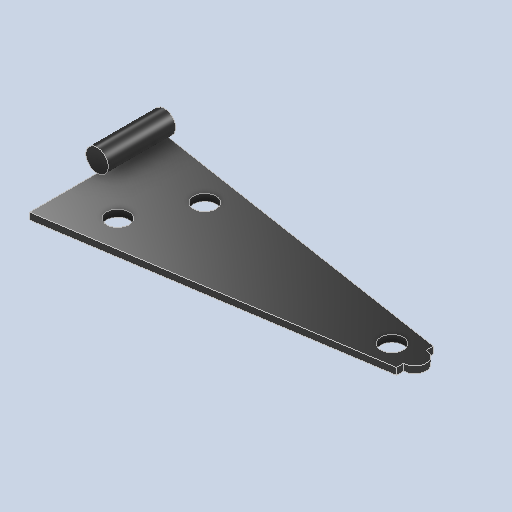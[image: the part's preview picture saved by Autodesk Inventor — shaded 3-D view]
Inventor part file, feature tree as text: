
AUTODESK INVENTOR PART (.ipt)
format: ipt  version: 2024 (Build 280153000, 153)  size: 113,664 bytes
history: native  units: in
note: dims shown in document units (in); Inventor stores cm internally (conversion verified against a paired STEP export)
features: other x3, sketch x2
ambient origin geometry x8: Origin, YZ Plane, XZ Plane, XY Plane, X Axis, Y Axis, Z Axis, Center Point
bodies: Solid1 (feature_tree)
feature tree (5):
  other  "Hinge.ipt"
  other  "Solid1::Hinge.ipt"
  other  "TaggingFeature1"
  sketch  "Sketch1"  dims[d0=0.3937in]
  sketch  "Sketch2"
